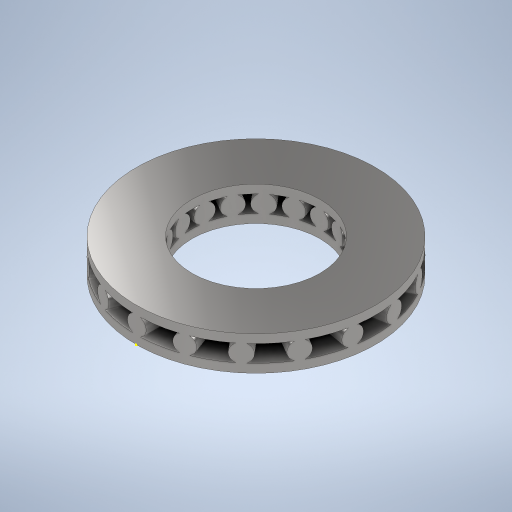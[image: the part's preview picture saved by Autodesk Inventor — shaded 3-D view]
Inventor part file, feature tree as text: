
AUTODESK INVENTOR PART (.ipt)
format: ipt  version: 2024.1 (Build 281209000, 209)  size: 465,920 bytes
history: native  units: in
note: dims shown in document units (in); Inventor stores cm internally (conversion verified against a paired STEP export)
features: sketch x5, extrude x4, plane x3, pattern_circular x1
ambient origin geometry x8: Origin, YZ Plane, XZ Plane, XY Plane, X Axis, Y Axis, Z Axis, Center Point
bodies: Solid1 (feature_tree)
feature tree (13):
  extrude  "Extrusion1"  Depth=0.5906in
  plane  "Work Plane1"
  extrude  "Extrusion2"  Depth=0.0866in
  pattern_circular  "Circular Pattern1"  Count=18 Angle=360.0deg
  sketch  "Sketch3"  dims[d5=0.0787in]
  plane  "Work Plane3"
  extrude  "Extrusion3"  Depth=0.0394in TaperAngle=0.0deg
  extrude  "Extrusion4"  Depth=0.1969in
  sketch  "Sketch1"  dims[d0=1.1024in d1=0.5906in]
  sketch  "Sketch2"  dims[d2=0.0394in d3=0.0in d4=0.0866in]
  plane  "Work Plane2"
  sketch  "Sketch4"  dims[d6=0.4562in d7=0.0in d8=7.0866in d9=360.0deg]
  sketch  "Sketch5"  dims[d11=-0.0039in d12=0.0394in d13=0.0in d14=0.1969in d15=0.0in d16=0.0in]
